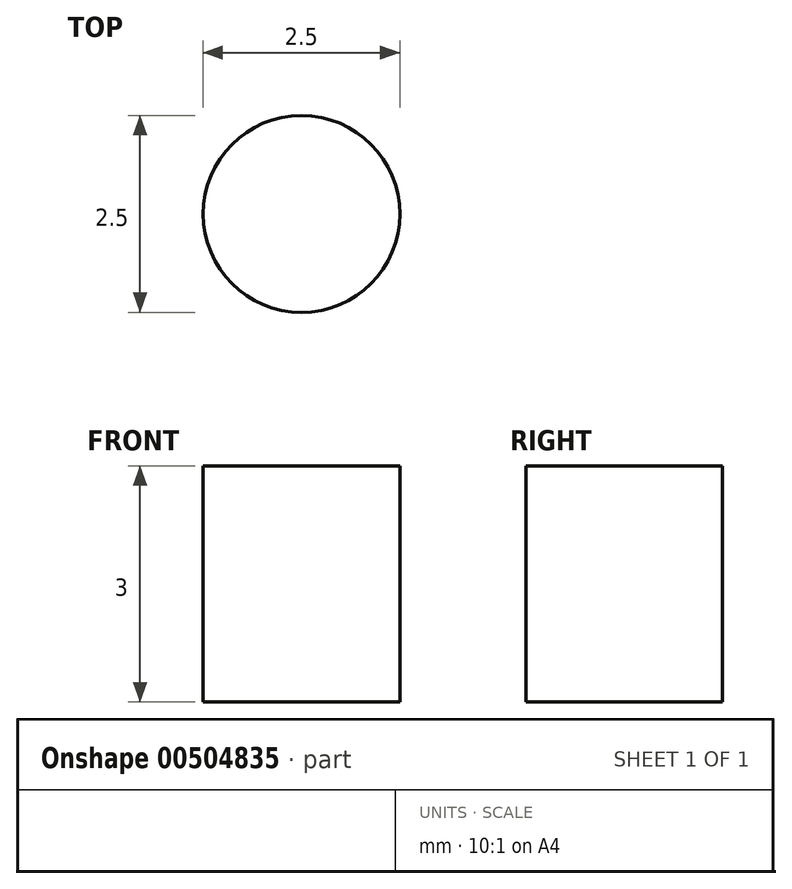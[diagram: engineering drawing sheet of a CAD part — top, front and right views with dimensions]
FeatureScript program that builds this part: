
annotation { "Feature Type Name" : "Feature", "Feature Type Description" : "" }
export const myFeature = defineFeature(function(context is Context, id is Id, definition is map)
    precondition{}
    {
        {
            var Q0;
            Q0=qCreatedBy(makeId("Top.planeOp"),FACE);
            var sketch = newSketch(context, id + "F0", { "sketchPlane" : qUnion([Q0])});
            skCircle(sketch, "E0", {"center": v(-14.35, 20.25) * mm, "radius": 1.25 * mm});
            skCircle(sketch, "E1", {"center": v(-20.35, 20.25) * mm, "radius": 1.25 * mm});
            skCircle(sketch, "E2", {"center": v(-8.35, -11.75) * mm, "radius": 1.6 * mm});
            skCircle(sketch, "E3", {"center": v(23.65, 20.25) * mm, "radius": 1.3 * mm});
            skCircle(sketch, "E4", {"center": v(-26.05, -22.65) * mm, "radius": 1.6 * mm});
            skCircle(sketch, "E5", {"center": v(7.65, 4.25) * mm, "radius": 19 * mm});
            skCircle(sketch, "E6", {"center": v(-26.05, -12.65) * mm, "radius": 1.6 * mm});
            skCircle(sketch, "E7", {"center": v(-8.35, 20.25) * mm, "radius": 1.3 * mm});
            skCircle(sketch, "E8", {"center": v(23.65, -11.75) * mm, "radius": 1.6 * mm});
            skLineSegment(sketch, "E9", {"start": v(27.65, -14.75) * mm, "end": v(27.65, -6.14) * mm});
            skLineSegment(sketch, "E10", {"start": v(18.04, -15.75) * mm, "end": v(26.65, -15.75) * mm});
            skLineSegment(sketch, "E11", {"start": v(-4.88, -15.75) * mm, "end": v(-2.74, -15.75) * mm});
            skLineSegment(sketch, "E12", {"start": v(-24.13, -25.7) * mm, "end": v(-11.28, -17.6) * mm});
            skLineSegment(sketch, "E13", {"start": v(-29.65, -12.65) * mm, "end": v(-29.65, -22.65) * mm});
            skLineSegment(sketch, "E14", {"start": v(-19.92, -4.53) * mm, "end": v(-27.97, -9.6) * mm});
            skLineSegment(sketch, "E15", {"start": v(-19.33, 16.25) * mm, "end": v(-20.35, 16.25) * mm});
            skLineSegment(sketch, "E16", {"start": v(-1.52, 24.25) * mm, "end": v(-20.35, 24.25) * mm});
            skLineSegment(sketch, "E17", {"start": v(26.65, 24.25) * mm, "end": v(16.82, 24.25) * mm});
            skLineSegment(sketch, "E18", {"start": v(27.65, 14.64) * mm, "end": v(27.65, 23.25) * mm});
            skArc(sketch, "E19", {"start": v(28.08, -3.92) * mm, "mid": v(27.76, -5) * mm, "end": v(27.65, -6.14) * mm});
            skArc(sketch, "E20", {"start": v(26.65, -15.75) * mm, "mid": v(27.36, -15.46) * mm, "end": v(27.65, -14.75) * mm});
            skArc(sketch, "E21", {"start": v(18.04, -15.75) * mm, "mid": v(16.9, -15.86) * mm, "end": v(15.82, -16.18) * mm});
            skArc(sketch, "E22", {"start": v(-0.52, -16.18) * mm, "mid": v(7.65, -17.75) * mm, "end": v(15.82, -16.18) * mm});
            skArc(sketch, "E23", {"start": v(-0.52, -16.18) * mm, "mid": v(-1.6, -15.86) * mm, "end": v(-2.74, -15.75) * mm});
            skArc(sketch, "E24", {"start": v(-4.88, -15.75) * mm, "mid": v(-8.21, -16.22) * mm, "end": v(-11.28, -17.6) * mm});
            skArc(sketch, "E25", {"start": v(-29.65, -22.65) * mm, "mid": v(-27.79, -25.8) * mm, "end": v(-24.13, -25.7) * mm});
            skArc(sketch, "E26", {"start": v(-27.97, -9.6) * mm, "mid": v(-29.2, -10.91) * mm, "end": v(-29.65, -12.65) * mm});
            skArc(sketch, "E27", {"start": v(-19.92, -4.53) * mm, "mid": v(-15.93, -0.39) * mm, "end": v(-14.33, 5.14) * mm});
            skArc(sketch, "E28", {"start": v(-14, 8.18) * mm, "mid": v(-14.22, 6.66) * mm, "end": v(-14.33, 5.14) * mm});
            skArc(sketch, "E29", {"start": v(-14, 8.18) * mm, "mid": v(-15.04, 13.28) * mm, "end": v(-19.33, 16.25) * mm});
            skArc(sketch, "E30", {"start": v(-20.35, 24.25) * mm, "mid": v(-24.35, 20.25) * mm, "end": v(-20.35, 16.25) * mm});
            skArc(sketch, "E31", {"start": v(16.82, 24.25) * mm, "mid": v(7.65, 26.25) * mm, "end": v(-1.52, 24.25) * mm});
            skArc(sketch, "E32", {"start": v(27.65, 23.25) * mm, "mid": v(27.36, 23.96) * mm, "end": v(26.65, 24.25) * mm});
            skArc(sketch, "E33", {"start": v(27.65, 14.64) * mm, "mid": v(27.76, 13.5) * mm, "end": v(28.08, 12.42) * mm});
            skArc(sketch, "E34", {"start": v(28.08, -3.92) * mm, "mid": v(29.65, 4.25) * mm, "end": v(28.08, 12.42) * mm});
            skSolve(sketch);
        }
        {
            var Q0;
            Q0=makeQuery(id+"F0.imprint","IMPRINT",FACE,{"disambiguationData":[TD([[makeQuery(id+"F0.imprint","IMPRINT",EDGE,{"derivedFrom":sQuery(id+"F0.wireOp",EDGE,"E0")}),1.0]])]});
            extrude(context, id + "F1", {"entities" : qUnion([Q0]), "depth" : 3 * mm, "offsetDistance" : 25 * mm});
        }
    });
